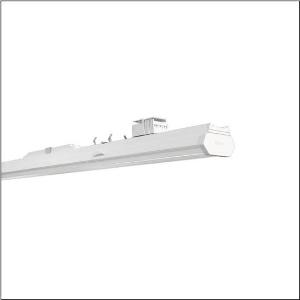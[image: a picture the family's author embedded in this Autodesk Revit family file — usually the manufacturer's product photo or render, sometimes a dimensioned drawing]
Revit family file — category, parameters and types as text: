
# Revit family: licross_r__21_protected_ho_52td12dn4e5m3s_02cf
name_source: partatom
category: Lighting Fixtures
units: mm (PartAtom-declared; Revit-internal decimal feet)

## family parameters
Cut with Voids When Loaded = No
Host = Face
Light Source = No
Part Type = Normal
Room Calculation Point = No
Round Connector Dimension = Use Diameter
Shared = No

## types (1)
- --- (1 x LED, 910 lm, 7.6 W, 4000K)
    Apparent Load = 8 VA
    CIE Flux Codes = 70 91 97 98 100
    Color Rendering = 80
    Color Temperature = 4000K
    Default Elevation = 1800 mm
    Description = Licross® 21 Protected HO, luminaire insert, of sheet steel, galvanised, coil coated, white, length: 1.500mm, width: 90mm, height: 103mm, LED rated luminous flux: 14.690lm, light colour: 840, control gear: DALI 2, with plug, 6-pole, with phase selection, for trunking rail, 14-core, mains connection: 220..240V, AC, 50/60Hz, rated input power: 89W, for trunking rail, 14-core, halogen-free wiring, for emergency light function, converter,control gear: single battery element, battery: LiFeP04, 9Ah, primary light control with lens, of plastic, primary optical cover: cover, of PMMA, light emission: direct distribution, primary light characteristic: symmetric, protection rating (complete): IP54, insulation class (complete): insulation class I (protective earthing), certification: CE, UKCA, protection symbol: D if used in an environment with non-conductive dust loads with corresponding accessories, impact resistance: IK06, permissible ambient temperature for indoor applications: +5..+30°C, standard: EN 60598-2-22, LABS conformity tested according to VDMA 24364:2018-05, reducing of maximum allowable ambient temperature of 5°C with ceiling mounting, corresponds to IFS (International Featured Standards) requirements for safety and quality in the food industry, packaging unit: 1 piece
    Height = 92 mm
    Lamp = 1 x LED
    Lamp Light Flux = 910 lm
    Lamp Power = 7.6 W
    Lamp count = 1
    Length = 1500 mm
    Luminous efficacy = 120 lm/W
    Manufacturer = Siteco
    ModVariant = No
    Model = 52TD12DN4E5M3S
    Mounting Place = Ceiling
    Mounting Type = Pendant
    Number of Poles = 1
    OnlyDefault = Yes
    Power Factor = 1
    Product Name = Licross® 21 Protected HO
    Product group = luminaire insert
    ProductGroupID = 901
    Protection Class = Protection class I
    Protection Degree = IP 54
    RLX_Detail_Level = 1
    RLX_Emergency_Light_Flux = 0 lm
    RLX_Emergency_Type = 0
    RLX_Emergency_Type_DB = No
    RlxData = <blob elided: 24825 chars, md5=fddc5c33>
    Socket = socket
    Standby Power = 0 W
    System Light Flux = 910 lm
    System Power = 8 W
    Type Comments = : emergency light operation: 3 h
    Type Image = l_1256148.jpg
    URL = http://relux.com
    VarID = @adj_059473
    Voltage = 0 V
    Weight = 0.00 kg
    Width = 88 mm

## geometry (parser evidence)
native form markers: Blend x4, Sweep x11
no freeform markers — native parametric forms only
